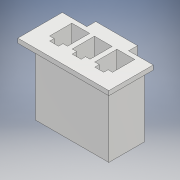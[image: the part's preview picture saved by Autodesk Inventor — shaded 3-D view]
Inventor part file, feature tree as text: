
AUTODESK INVENTOR PART (.ipt)
format: ipt  version: 2017 (Build 210142000, 142)  size: 219,648 bytes
history: native  units: mm
features: other x6, extrude x5, sketch x5, pattern_linear x1
ambient origin geometry x8: Origin, YZ Plane, XZ Plane, XY Plane, X Axis, Y Axis, Z Axis, Center Point
bodies: Solide1 (feature_tree)
feature tree (17):
  other  "Table"
  other  "Connecteur JST 3 Broches Male"
  other  "Connecteur JST 4 Broches Male"
  other  "Connecteur JST 2 Broches Male"
  other  "Connecteur JST 5 Broches Male"
  other  "Connecteur JST 6 Broches Male"
  extrude  "Embase"  Depth=8.24mm
  extrude  "Epaulement"  Depth=4.0mm
  extrude  "Clip"  Depth=7.5mm TaperAngle=0.0deg
  extrude  "Extrusion4"  Depth=5.0mm
  extrude  "Extrusion5"  Depth=0.5mm TaperAngle=0.0deg
  pattern_linear  "Réseau rectangulaire1"  Spacing1=1.0mm  [1 undecoded]
  sketch  "Esquisse1"
  sketch  "Esquisse2"
  sketch  "Esquisse4"
  sketch  "Esquisse5"
  sketch  "Esquisse6"
note: 1 required parameter value undecoded (feature->parameter linkage not recoverable at this tier; creation-order binding heuristic only, values carry confidence <= 0.55)
